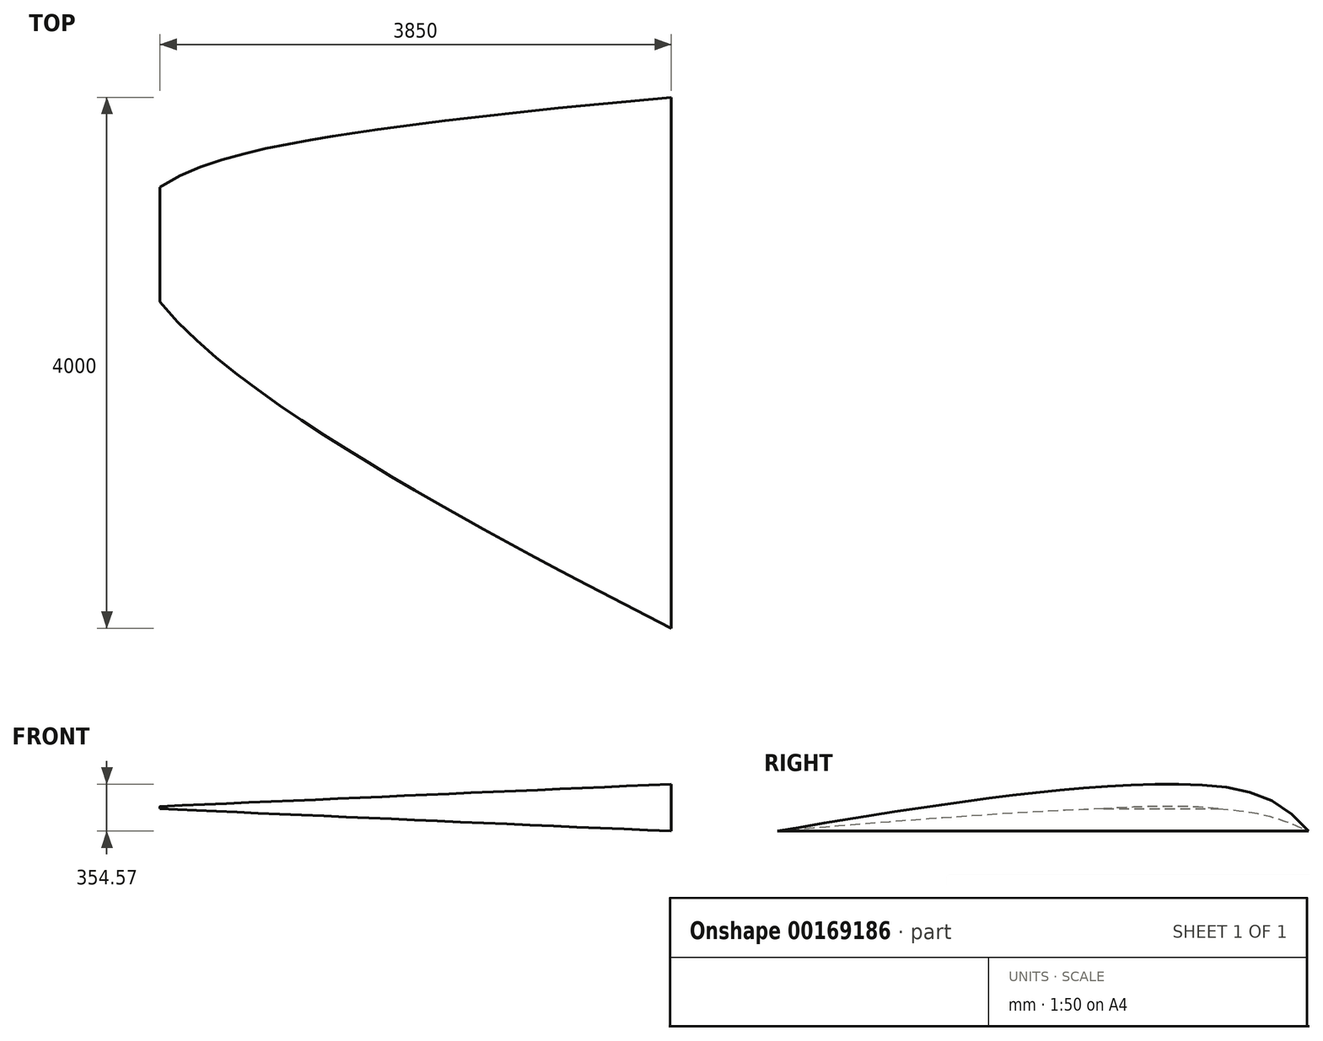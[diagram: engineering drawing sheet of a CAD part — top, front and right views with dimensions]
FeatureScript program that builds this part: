
annotation { "Feature Type Name" : "Feature", "Feature Type Description" : "" }
export const myFeature = defineFeature(function(context is Context, id is Id, definition is map)
    precondition{}
    {
        {
            var Q0;
            Q0=qCreatedBy(makeId("Right.planeOp"),FACE);
            var sketch = newSketch(context, id + "F0", { "sketchPlane" : qUnion([Q0])});
            skLineSegment(sketch, "E0", {"start": v(-2000, 0) * mm, "end": v(2000, 0) * mm});
            skFitSpline(sketch, "E1", {"points": [v(2000, 0) * mm, v(1150, 350) * mm, v(-2000, 0) * mm], "startDerivative": vector(-1838.86, 2296.85) * mm, "endDerivative": vector(-6608.78, -1143.42) * mm});
            skSolve(sketch);
        }
        {
            var Q0;
            Q0=makeQuery(id+"F0.imprint","IMPRINT",FACE,{"disambiguationData":[TD([[makeQuery(id+"F0.imprint","IMPRINT",EDGE,{"derivedFrom":sQuery(id+"F0.wireOp",EDGE,"E0")}),1.0]])]});
            extrude(context, id + "F1", {"entities" : qUnion([Q0]), "oppositeDirection" : true, "depth" : 3850 * mm, "hasDraft" : true, "draftAngle" : 2.5 * degree, "draftPullDirection" : true});
        }
    });
